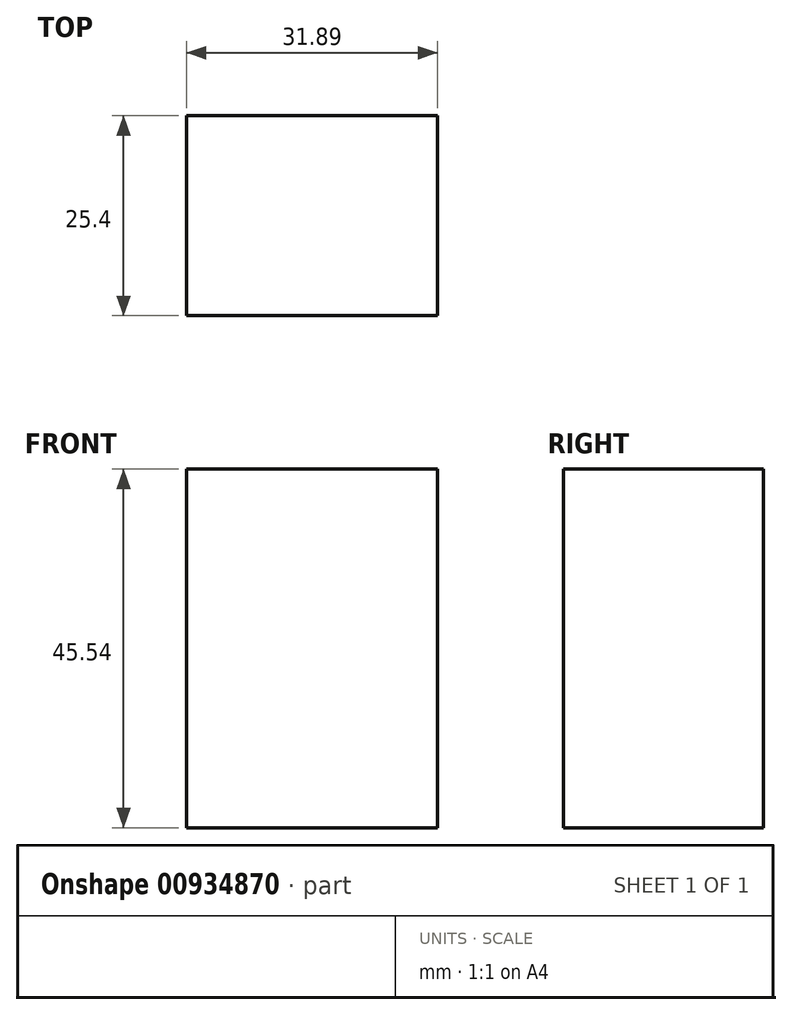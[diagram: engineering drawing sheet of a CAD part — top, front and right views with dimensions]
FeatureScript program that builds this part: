
annotation { "Feature Type Name" : "Feature", "Feature Type Description" : "" }
export const myFeature = defineFeature(function(context is Context, id is Id, definition is map)
    precondition{}
    {
        {
            var Q0;
            Q0=qCreatedBy(makeId("Front.planeOp"),FACE);
            var sketch = newSketch(context, id + "F0", { "sketchPlane" : qUnion([Q0])});
            skLineSegment(sketch, "E0.bottom", {"start": v(0, 57) * mm, "end": v(-31.9, 57) * mm});
            skLineSegment(sketch, "E0.top", {"start": v(0, 102.55) * mm, "end": v(-31.9, 102.55) * mm});
            skLineSegment(sketch, "E0.left", {"start": v(0, 57) * mm, "end": v(0, 102.55) * mm});
            skLineSegment(sketch, "E0.right", {"start": v(-31.9, 57) * mm, "end": v(-31.9, 102.55) * mm});
            skSolve(sketch);
        }
        {
            var Q0;
            Q0=makeQuery(id+"F0.imprint","IMPRINT",FACE,{"disambiguationData":[TD([[makeQuery(id+"F0.imprint","IMPRINT",EDGE,{"derivedFrom":sQuery(id+"F0.wireOp",EDGE,"E0.bottom")}),-1.0]])]});
            extrude(context, id + "F1", {"entities" : qUnion([Q0]), "depth" : 25.4 * mm, "offsetDistance" : 25.4 * mm});
        }
    });
